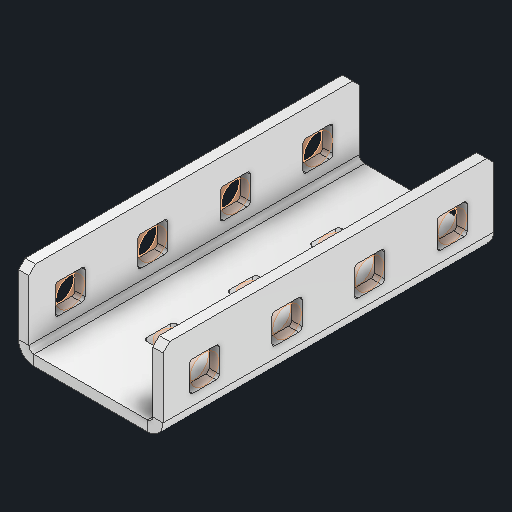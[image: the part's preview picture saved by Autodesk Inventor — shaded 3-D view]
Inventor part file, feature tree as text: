
AUTODESK INVENTOR PART (.ipt)
format: ipt  version: 2025 (Build 290162000, 162)  size: 350,208 bytes
history: native  units: in
note: dims shown in document units (in); Inventor stores cm internally (conversion verified against a paired STEP export)
features: other x27, sketch x3
ambient origin geometry x8: Origin, YZ Plane, XZ Plane, XY Plane, X Axis, Y Axis, Z Axis, Center Point
bodies: Solid1 (feature_tree)
feature tree (30):
  other  "C Channel Coupler.ipt"
  other  "Solid1::C Channel Coupler.ipt"
  other  "TaggingFeature1"
  sketch  "Sketch1"  dims[d0=0.3937in]
  sketch  "Sketch2"  dims[d1=0.0625in]
  sketch  "Sketch3"
  other  "Flange Pattern Sketch"
  other  "Flange Pattern Plane"
  other  "Srf1"
  other  "Srf2"
  other  "Srf3"
  other  "Srf4"
  other  "Srf5"
  other  "Srf6"
  other  "Srf7"
  other  "Srf8"
  other  "Srf9"
  other  "Srf10"
  other  "Srf11"
  other  "Srf1::Derived"
  other  "Srf2::Derived"
  other  "Srf823::Derived"
  other  "Srf824::Derived"
  other  "Srf825::Derived"
  other  "Srf826::Derived"
  other  "Srf827::Derived"
  other  "Srf828::Derived"
  other  "Srf786::Derived"
  other  "Srf889::Derived"
  other  "Srf890::Derived"
